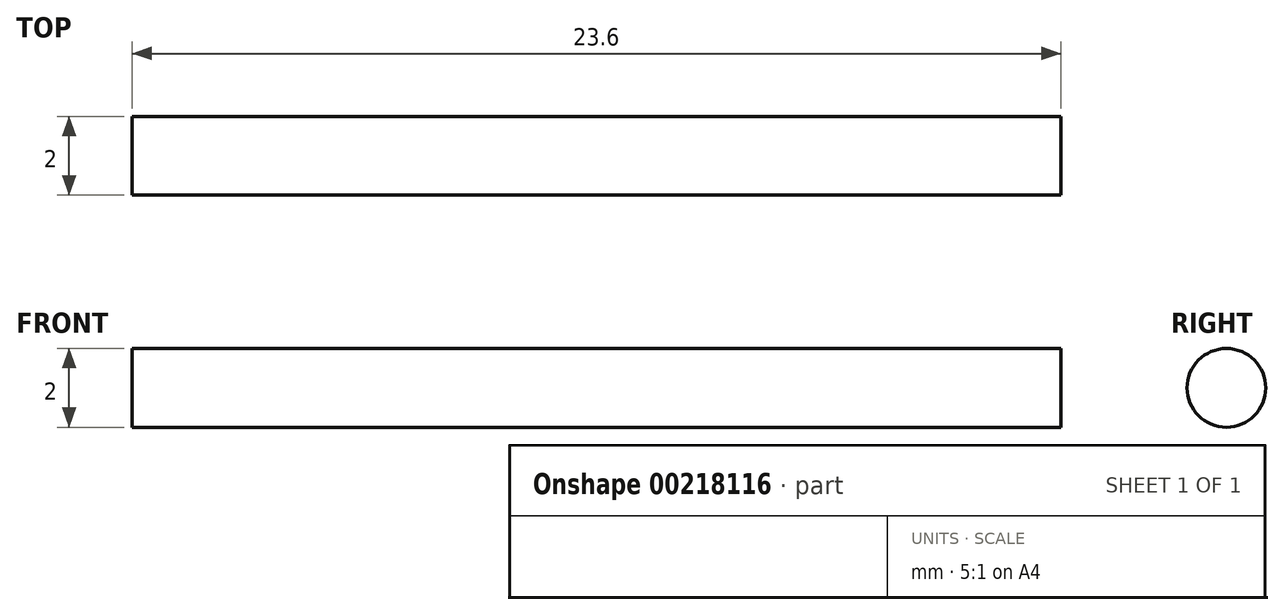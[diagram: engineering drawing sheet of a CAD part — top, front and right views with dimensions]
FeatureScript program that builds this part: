
annotation { "Feature Type Name" : "Feature", "Feature Type Description" : "" }
export const myFeature = defineFeature(function(context is Context, id is Id, definition is map)
    precondition{}
    {
        {
            var Q0;
            Q0=qCreatedBy(makeId("Right.planeOp"),FACE);
            var sketch = newSketch(context, id + "F0", { "sketchPlane" : qUnion([Q0])});
            skCircle(sketch, "E0", {"center": v(0, 0) * mm, "radius": 1 * mm});
            skSolve(sketch);
        }
        {
            var Q0;
            Q0=makeQuery(id+"F0.imprint","IMPRINT",FACE,{"disambiguationData":[TD([[makeQuery(id+"F0.imprint","IMPRINT",EDGE,{"derivedFrom":sQuery(id+"F0.wireOp",EDGE,"E0")}),1.0]])]});
            extrude(context, id + "F1", {"entities" : qUnion([Q0]), "depth" : 23.6 * mm});
        }
    });
